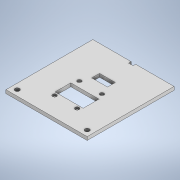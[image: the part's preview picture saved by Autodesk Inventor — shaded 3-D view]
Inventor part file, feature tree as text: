
AUTODESK INVENTOR PART (.ipt)
format: ipt  version: 2021 (Build 250183000, 183)  size: 189,952 bytes
history: native  units: mm
features: thread x6, extrude x3, other x1, sketch x1
ambient origin geometry x8: Origin, YZ Plane, XZ Plane, XY Plane, X Axis, Y Axis, Z Axis, Center Point
bodies: Body1 (feature_tree)
feature tree (11):
  other  "Sólido1"
  sketch  "Boceto1"  dims[d0=36.0mm d1=0.0mm d2=77.0mm d3=0.0mm d4=72.0mm d5=5.0mm d6=5.0mm d7=0.0mm d8=5.0mm d9=5.0mm d10=4.0mm d11=4.0mm d12=3.0mm d13=0.0mm d14=36.0mm d15=2.25mm d16=2.0mm d17=2.0mm d18=50.0mm d19=25.0mm d20=14.0mm d21=5.4mm d22=2.5mm d23=2.5mm d24=2.5mm d25=2.5mm d26=3.5mm d27=3.5mm d28=27.0mm d29=25.0mm d30=2.5mm d31=2.5mm d32=2.5mm d33=2.5mm d34=3.5mm d35=3.5mm d36=1.5mm d37=0.0mm d38=3.0mm d39=0.0mm d40=3.0mm d41=0.0mm d42=1.5mm d43=0.0mm d44=1.5mm d45=0.0mm d46=1.5mm d47=0.0mm d48=1.5mm d49=0.0mm d50=8.0mm d51=8.0mm d52=1.0mm d53=0.0mm d61=30.0mm d63=7.0mm d64=14.0mm d65=7.0mm d66=0.0mm]
  extrude  "Extrusión1"  TaperAngle=0.0deg  [1 undecoded]
  extrude  "Extrusión2"  Depth=77.0mm
  thread  "Rosca1"  [1 undecoded]
  thread  "Rosca2"  [1 undecoded]
  thread  "Rosca3"  [1 undecoded]
  thread  "Rosca4"  [1 undecoded]
  thread  "Rosca5"  [1 undecoded]
  thread  "Rosca6"  [1 undecoded]
  extrude  "Extrusión3"  Depth=5.0mm
note: 7 required parameter values undecoded (feature->parameter linkage not recoverable at this tier; creation-order binding heuristic only, values carry confidence <= 0.55)
